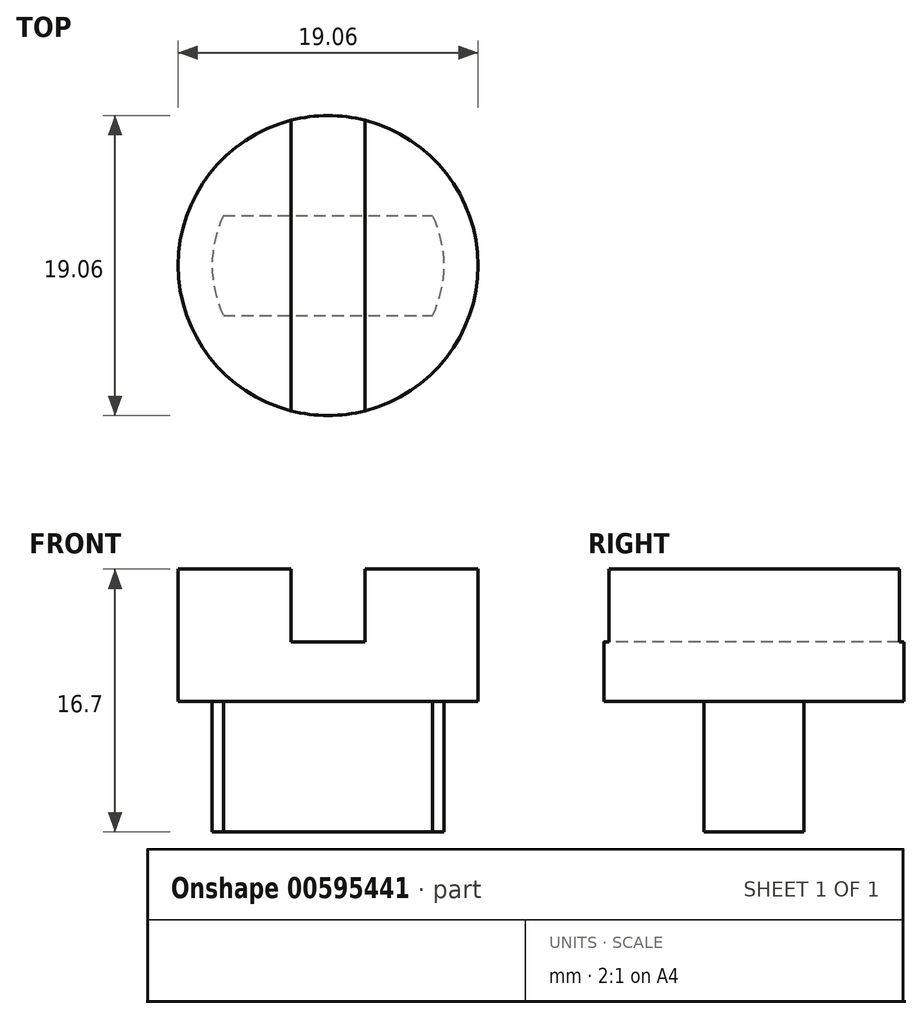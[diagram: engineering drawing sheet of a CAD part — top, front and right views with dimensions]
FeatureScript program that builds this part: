
annotation { "Feature Type Name" : "Feature", "Feature Type Description" : "" }
export const myFeature = defineFeature(function(context is Context, id is Id, definition is map)
    precondition{}
    {
        {
            var Q0;
            Q0=qCreatedBy(makeId("Top.planeOp"),FACE);
            var sketch = newSketch(context, id + "F0", { "sketchPlane" : qUnion([Q0])});
            skCircle(sketch, "E0", {"center": v(0, 0) * mm, "radius": 9.53 * mm});
            skSolve(sketch);
        }
        {
            var Q0;
            Q0=makeQuery(id+"F0.imprint","IMPRINT",FACE,{"disambiguationData":[TD([[makeQuery(id+"F0.imprint","IMPRINT",EDGE,{"derivedFrom":sQuery(id+"F0.wireOp",EDGE,"E0")}),1.0]])]});
            extrude(context, id + "F1", {"entities" : qUnion([Q0]), "depth" : 16.7 * mm, "offsetDistance" : 25.4 * mm});
        }
        {
            var Q0;
            Q0=makeQuery(id+"F1.opExtrude","CAP_FACE",FACE,{"disambiguationData":[OSD([sQuery(id+"F0.wireOp",EDGE,"E0")])],"isStart":false});
            var sketch = newSketch(context, id + "F2", { "sketchPlane" : qUnion([Q0])});
            skLineSegment(sketch, "E1", {"start": v(-2.35, 9.23) * mm, "end": v(-2.35, -9.23) * mm});
            skLineSegment(sketch, "E2", {"start": v(2.35, 9.23) * mm, "end": v(2.35, -9.23) * mm});
            skSolve(sketch);
        }
        {
            var Q0;
            {var subQ0=sQuery(id+"F2.wireOp",EDGE,"E1");Q0=makeQuery(id+"F2.imprint","IMPRINT",FACE,{"disambiguationData":[TD([[makeQuery(id+"F2.imprint","IMPRINT",EDGE,{"derivedFrom":subQ0}),1.0]])]});}
            extrude(context, id + "F3", {"entities" : qUnion([Q0]), "operationType" : NewBodyOperationType.REMOVE, "oppositeDirection" : true, "depth" : 4.62 * mm, "offsetDistance" : 25.4 * mm});
        }
        {
            var Q0;
            Q0=makeQuery(id+"F1.opExtrude","CAP_FACE",FACE,{"disambiguationData":[OSD([sQuery(id+"F0.wireOp",EDGE,"E0")])],"isStart":true});
            var sketch = newSketch(context, id + "F4", { "sketchPlane" : qUnion([Q0])});
            skArc(sketch, "E3", {"start": v(-6.65, 3.17) * mm, "mid": v(-7.37, 0) * mm, "end": v(-6.65, -3.18) * mm});
            skLineSegment(sketch, "E4", {"start": v(-6.65, 3.18) * mm, "end": v(6.65, 3.18) * mm});
            skLineSegment(sketch, "E5", {"start": v(-6.65, -3.18) * mm, "end": v(6.65, -3.18) * mm});
            skArc(sketch, "E6.trimOffspring", {"start": v(6.65, -3.18) * mm, "mid": v(7.37, 0) * mm, "end": v(6.65, 3.18) * mm});
            skSolve(sketch);
        }
        {
            var Q0;
            Q0=makeQuery(id+"F4.imprint","IMPRINT",FACE,{"disambiguationData":[TD([[makeQuery(id+"F4.imprint","IMPRINT",EDGE,{"derivedFrom":sQuery(id+"F4.wireOp",EDGE,"E3")}),-1.0]])]});
            extrude(context, id + "F5", {"entities" : qUnion([Q0]), "operationType" : NewBodyOperationType.REMOVE, "oppositeDirection" : true, "depth" : 8.28 * mm, "offsetDistance" : 25.4 * mm});
        }
    });
